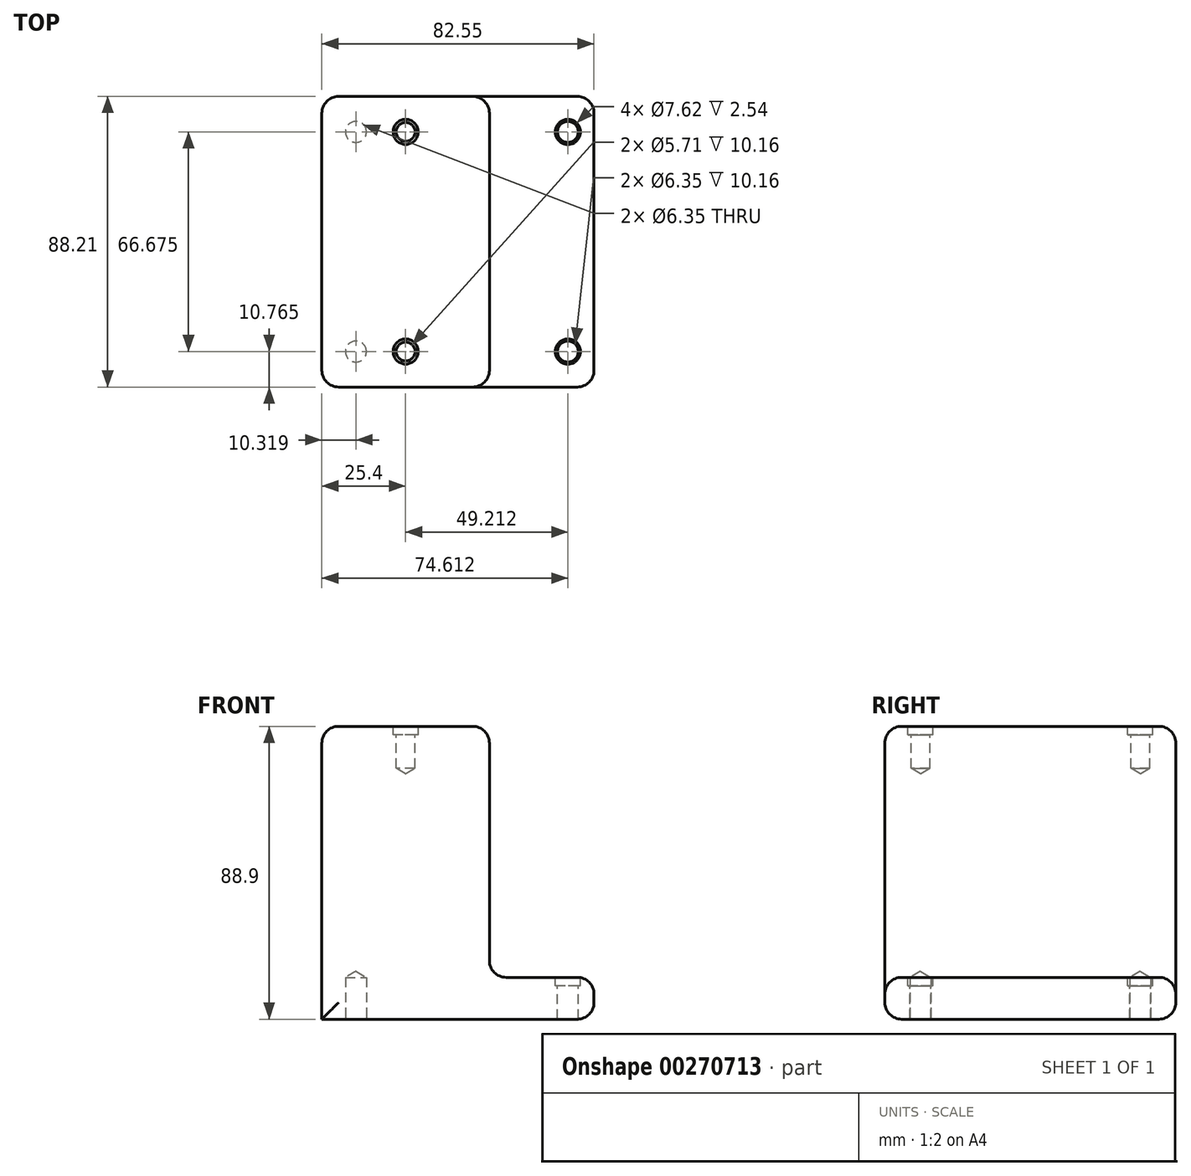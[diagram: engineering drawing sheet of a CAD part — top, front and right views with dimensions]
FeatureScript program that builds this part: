
annotation { "Feature Type Name" : "Feature", "Feature Type Description" : "" }
export const myFeature = defineFeature(function(context is Context, id is Id, definition is map)
    precondition{}
    {
        {
            var Q0;
            Q0=qCreatedBy(makeId("Front.planeOp"),FACE);
            var sketch = newSketch(context, id + "F0", { "sketchPlane" : qUnion([Q0])});
            skLineSegment(sketch, "E0.bottom", {"start": v(0, 0) * mm, "end": v(82.55, 0) * mm});
            skLineSegment(sketch, "E0.top", {"start": v(0, 88.9) * mm, "end": v(50.8, 88.9) * mm});
            skLineSegment(sketch, "E0.left", {"start": v(0, 0) * mm, "end": v(0, 88.9) * mm});
            skLineSegment(sketch, "E0.right", {"start": v(82.55, 0) * mm, "end": v(82.55, 12.7) * mm});
            skLineSegment(sketch, "E1", {"start": v(50.8, 88.9) * mm, "end": v(50.8, 12.7) * mm});
            skLineSegment(sketch, "E2", {"start": v(50.8, 12.7) * mm, "end": v(82.55, 12.7) * mm});
            skSolve(sketch);
        }
        {
            var Q0;
            Q0 = qSketchRegion(id + "F0", true);
            extrude(context, id + "F1", {"entities" : qUnion([Q0]), "depth" : 88.2 * mm});
        }
        {
            var Q0;
            Q0=makeQuery(id+"F1.opExtrude","SWEPT_FACE",FACE,{"disambiguationData":[OSD([sQuery(id+"F0.wireOp",EDGE,"E0.top")])]});
            var sketch = newSketch(context, id + "F2", { "sketchPlane" : qUnion([Q0])});
            skPoint(sketch, "E3", {"position": v(25.4, -10.77) * mm});
            skPoint(sketch, "E4", {"position": v(25.4, -77.44) * mm});
            skSolve(sketch);
        }
        {
            var Q0;
            Q0=sQuery(id+"F2.wireOp",VERTEX,"E4");
            var Q1;
            Q1=sQuery(id+"F2.wireOp",VERTEX,"E3");
            var Q2;
            Q2=makeQuery(id+"F1.opExtrude","SWEPT_BODY",BODY,{"disambiguationData":[OSD([sQuery(id+"F0.wireOp",EDGE,"E0.bottom"),sQuery(id+"F0.wireOp",EDGE,"E0.left"),sQuery(id+"F0.wireOp",EDGE,"E0.right"),sQuery(id+"F0.wireOp",EDGE,"E0.top"),sQuery(id+"F0.wireOp",EDGE,"E1"),sQuery(id+"F0.wireOp",EDGE,"E2")])]});
            hole(context, id + "F3", {"style" : HoleStyle.C_BORE, "endStyle" : HoleEndStyle.BLIND, "holeDiameter" : 5.7 * mm, "cBoreDiameter" : 7.62 * mm, "cBoreDepth" : 2.54 * mm, "holeDepth" : 12.7 * mm, "tappedDepth" : 12.7 * mm, "tapClearance" : 3, "locations" : qUnion([Q0, Q1]), "scope" : qUnion([Q2])});
        }
        {
            var Q0;
            Q0=makeQuery(id+"F1.opExtrude","SWEPT_FACE",FACE,{"disambiguationData":[OSD([sQuery(id+"F0.wireOp",EDGE,"E2")])]});
            var sketch = newSketch(context, id + "F4", { "sketchPlane" : qUnion([Q0])});
            skPoint(sketch, "E5", {"position": v(74.61, -77.44) * mm});
            skPoint(sketch, "E6", {"position": v(74.61, -10.77) * mm});
            skSolve(sketch);
        }
        {
            var Q0;
            Q0=sQuery(id+"F4.wireOp",VERTEX,"E6");
            var Q1;
            Q1=sQuery(id+"F4.wireOp",VERTEX,"E5");
            var Q2;
            Q2=makeQuery(id+"F1.opExtrude","SWEPT_BODY",BODY,{"disambiguationData":[OSD([sQuery(id+"F0.wireOp",EDGE,"E0.bottom"),sQuery(id+"F0.wireOp",EDGE,"E0.left"),sQuery(id+"F0.wireOp",EDGE,"E0.right"),sQuery(id+"F0.wireOp",EDGE,"E0.top"),sQuery(id+"F0.wireOp",EDGE,"E1"),sQuery(id+"F0.wireOp",EDGE,"E2")])]});
            hole(context, id + "F5", {"style" : HoleStyle.C_BORE, "endStyle" : HoleEndStyle.BLIND, "holeDiameter" : 6.35 * mm, "cBoreDiameter" : 7.62 * mm, "cBoreDepth" : 2.54 * mm, "holeDepth" : 12.7 * mm, "tappedDepth" : 12.7 * mm, "tapClearance" : 3, "locations" : qUnion([Q0, Q1]), "scope" : qUnion([Q2])});
        }
        {
            var Q0;
            Q0=makeQuery(id+"F1.opExtrude","SWEPT_FACE",FACE,{"disambiguationData":[OSD([sQuery(id+"F0.wireOp",EDGE,"E0.bottom")])]});
            var sketch = newSketch(context, id + "F6", { "sketchPlane" : qUnion([Q0])});
            skLineSegment(sketch, "E7", {"start": v(0, 0) * mm, "end": v(82.55, 0) * mm});
            skLineSegment(sketch, "E8", {"start": v(0, 88.21) * mm, "end": v(82.55, 88.21) * mm});
            skPoint(sketch, "E9", {"position": v(10.32, 77.44) * mm});
            skPoint(sketch, "E10", {"position": v(10.32, 10.77) * mm});
            skLineSegment(sketch, "E11", {"start": v(74.61, 77.44) * mm, "end": v(74.61, 10.77) * mm});
            skSolve(sketch);
        }
        {
            var Q0;
            Q0=sQuery(id+"F6.wireOp",VERTEX,"E9");
            var Q1;
            Q1=sQuery(id+"F6.wireOp",VERTEX,"E10");
            var Q2;
            Q2=makeQuery(id+"F1.opExtrude","SWEPT_BODY",BODY,{"disambiguationData":[OSD([sQuery(id+"F0.wireOp",EDGE,"E0.bottom"),sQuery(id+"F0.wireOp",EDGE,"E0.left"),sQuery(id+"F0.wireOp",EDGE,"E0.right"),sQuery(id+"F0.wireOp",EDGE,"E0.top"),sQuery(id+"F0.wireOp",EDGE,"E1"),sQuery(id+"F0.wireOp",EDGE,"E2")])]});
            hole(context, id + "F7", {"style" : HoleStyle.SIMPLE, "endStyle" : HoleEndStyle.BLIND, "holeDiameter" : 6.35 * mm, "holeDepth" : 12.7 * mm, "tappedDepth" : 12.7 * mm, "tapClearance" : 3, "locations" : qUnion([Q0, Q1]), "scope" : qUnion([Q2])});
        }
        {
            var Q0;
            Q0=makeQuery(id+"F1.opExtrude","SWEPT_EDGE",EDGE,{"disambiguationData":[OSD([sQuery(id+"F0.wireOp",EDGE,"E0.top"),sQuery(id+"F0.wireOp",EDGE,"E1")])]});
            var Q1;
            Q1=makeQuery(id+"F1.opExtrude","SWEPT_EDGE",EDGE,{"disambiguationData":[OSD([sQuery(id+"F0.wireOp",EDGE,"E0.left"),sQuery(id+"F0.wireOp",EDGE,"E0.top")])]});
            var Q2;
            Q2=makeQuery(id+"F1.opExtrude","CAP_EDGE",EDGE,{"disambiguationData":[OSD([sQuery(id+"F0.wireOp",EDGE,"E0.top")])],"isStart":false});
            var Q3;
            Q3=makeQuery(id+"F1.opExtrude","CAP_EDGE",EDGE,{"disambiguationData":[OSD([sQuery(id+"F0.wireOp",EDGE,"E0.top")])],"isStart":true});
            var Q4;
            Q4=makeQuery(id+"F1.opExtrude","CAP_EDGE",EDGE,{"disambiguationData":[OSD([sQuery(id+"F0.wireOp",EDGE,"E1")])],"isStart":false});
            var Q5;
            Q5=makeQuery(id+"F1.opExtrude","CAP_EDGE",EDGE,{"disambiguationData":[OSD([sQuery(id+"F0.wireOp",EDGE,"E2")])],"isStart":false});
            var Q6;
            Q6=makeQuery(id+"F1.opExtrude","SWEPT_EDGE",EDGE,{"disambiguationData":[OSD([sQuery(id+"F0.wireOp",EDGE,"E0.right"),sQuery(id+"F0.wireOp",EDGE,"E2")])]});
            var Q7;
            Q7=makeQuery(id+"F1.opExtrude","CAP_EDGE",EDGE,{"disambiguationData":[OSD([sQuery(id+"F0.wireOp",EDGE,"E2")])],"isStart":true});
            var Q8;
            Q8=makeQuery(id+"F1.opExtrude","CAP_EDGE",EDGE,{"disambiguationData":[OSD([sQuery(id+"F0.wireOp",EDGE,"E1")])],"isStart":true});
            var Q9;
            Q9=makeQuery(id+"F1.opExtrude","SWEPT_EDGE",EDGE,{"disambiguationData":[OSD([sQuery(id+"F0.wireOp",EDGE,"E0.bottom"),sQuery(id+"F0.wireOp",EDGE,"E0.right")])]});
            var Q10;
            Q10=makeQuery(id+"F1.opExtrude","CAP_EDGE",EDGE,{"disambiguationData":[OSD([sQuery(id+"F0.wireOp",EDGE,"E0.right")])],"isStart":false});
            var Q11;
            Q11=makeQuery(id+"F1.opExtrude","CAP_EDGE",EDGE,{"disambiguationData":[OSD([sQuery(id+"F0.wireOp",EDGE,"E0.right")])],"isStart":true});
            var Q12;
            Q12=makeQuery(id+"F1.opExtrude","CAP_EDGE",EDGE,{"disambiguationData":[OSD([sQuery(id+"F0.wireOp",EDGE,"E0.bottom")])],"isStart":true});
            var Q13;
            Q13=makeQuery(id+"F1.opExtrude","CAP_EDGE",EDGE,{"disambiguationData":[OSD([sQuery(id+"F0.wireOp",EDGE,"E0.left")])],"isStart":true});
            var Q14;
            Q14=makeQuery(id+"F1.opExtrude","CAP_EDGE",EDGE,{"disambiguationData":[OSD([sQuery(id+"F0.wireOp",EDGE,"E0.left")])],"isStart":false});
            var Q15;
            Q15=makeQuery(id+"F1.opExtrude","CAP_EDGE",EDGE,{"disambiguationData":[OSD([sQuery(id+"F0.wireOp",EDGE,"E0.bottom")])],"isStart":false});
            var Q16;
            Q16=makeQuery(id+"F1.opExtrude","SWEPT_EDGE",EDGE,{"disambiguationData":[OSD([sQuery(id+"F0.wireOp",EDGE,"E1"),sQuery(id+"F0.wireOp",EDGE,"E2")])]});
            fillet(context, id + "F8", {"entities" : qUnion([Q0, Q1, Q2, Q3, Q4, Q5, Q6, Q7, Q8, Q9, Q10, Q11, Q12, Q13, Q14, Q15, Q16]), "radius" : 5.08 * mm, "tangentPropagation" : true, "allowEdgeOverflow" : false});
        }
    });
